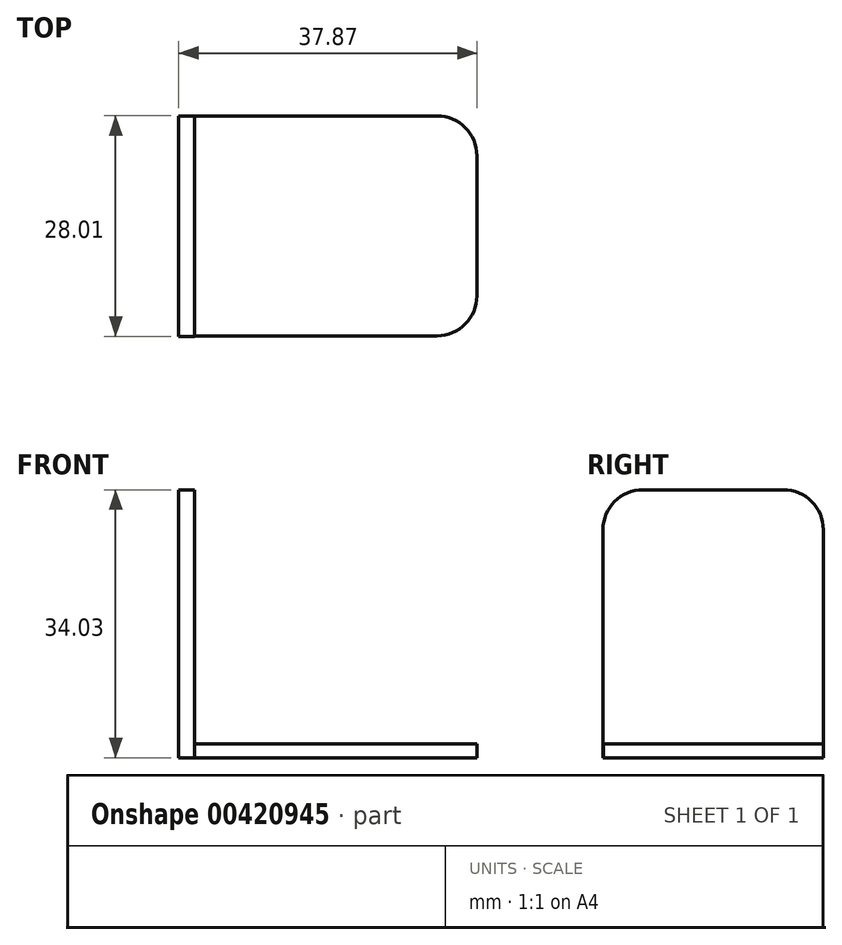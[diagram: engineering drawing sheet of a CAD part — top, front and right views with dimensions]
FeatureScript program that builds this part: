
annotation { "Feature Type Name" : "Feature", "Feature Type Description" : "" }
export const myFeature = defineFeature(function(context is Context, id is Id, definition is map)
    precondition{}
    {
        {
            var Q0;
            Q0=qCreatedBy(makeId("Top.planeOp"),FACE);
            var sketch = newSketch(context, id + "F0", { "sketchPlane" : qUnion([Q0])});
            skLineSegment(sketch, "E0.bottom", {"start": v(12.89, 52.07) * mm, "end": v(48.73, 52.07) * mm});
            skLineSegment(sketch, "E0.top", {"start": v(12.89, 24.12) * mm, "end": v(48.73, 24.12) * mm});
            skLineSegment(sketch, "E0.left", {"start": v(12.89, 52.07) * mm, "end": v(12.89, 24.12) * mm});
            skLineSegment(sketch, "E0.right", {"start": v(48.73, 52.07) * mm, "end": v(48.73, 24.12) * mm});
            skSolve(sketch);
        }
        {
            var Q0;
            Q0 = qSketchRegion(id + "F0", true);
            extrude(context, id + "F1", {"entities" : qUnion([Q0]), "depth" : 1.78 * mm});
        }
        {
            var Q0;
            Q0=makeQuery(id+"F1.opExtrude","SWEPT_EDGE",EDGE,{"disambiguationData":[OSD([sQuery(id+"F0.wireOp",EDGE,"E0.top"),sQuery(id+"F0.wireOp",EDGE,"E0.right")])]});
            var Q1;
            Q1=makeQuery(id+"F1.opExtrude","SWEPT_EDGE",EDGE,{"disambiguationData":[OSD([sQuery(id+"F0.wireOp",EDGE,"E0.bottom"),sQuery(id+"F0.wireOp",EDGE,"E0.right")])]});
            fillet(context, id + "F2", {"entities" : qUnion([Q0, Q1]), "radius" : 5.08 * mm, "tangentPropagation" : true, "allowEdgeOverflow" : false});
        }
        {
            var Q0;
            Q0=makeQuery(id+"F1.opExtrude","SWEPT_FACE",FACE,{"disambiguationData":[OSD([sQuery(id+"F0.wireOp",EDGE,"E0.left")])]});
            var sketch = newSketch(context, id + "F3", { "sketchPlane" : qUnion([Q0])});
            skLineSegment(sketch, "E1.bottom", {"start": v(-52.07, 0) * mm, "end": v(-24.06, 0) * mm});
            skLineSegment(sketch, "E1.top", {"start": v(-52.07, 34.03) * mm, "end": v(-24.06, 34.03) * mm});
            skLineSegment(sketch, "E1.left", {"start": v(-52.07, 0) * mm, "end": v(-52.07, 34.03) * mm});
            skLineSegment(sketch, "E1.right", {"start": v(-24.06, 0) * mm, "end": v(-24.06, 34.03) * mm});
            skSolve(sketch);
        }
        {
            var Q0;
            Q0 = qSketchRegion(id + "F3", true);
            extrude(context, id + "F4", {"entities" : qUnion([Q0]), "operationType" : NewBodyOperationType.ADD, "depth" : 2.03 * mm});
        }
        {
            var Q0;
            Q0=makeQuery(id+"F4.opExtrude","SWEPT_EDGE",EDGE,{"disambiguationData":[OSD([sQuery(id+"F3.wireOp",EDGE,"E1.top"),sQuery(id+"F3.wireOp",EDGE,"E1.left")])]});
            var Q1;
            Q1=makeQuery(id+"F4.opExtrude","SWEPT_EDGE",EDGE,{"disambiguationData":[OSD([sQuery(id+"F3.wireOp",EDGE,"E1.top"),sQuery(id+"F3.wireOp",EDGE,"E1.right")])]});
            fillet(context, id + "F5", {"entities" : qUnion([Q0, Q1]), "radius" : 5.08 * mm, "tangentPropagation" : true, "allowEdgeOverflow" : false});
        }
    });
